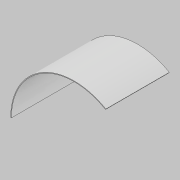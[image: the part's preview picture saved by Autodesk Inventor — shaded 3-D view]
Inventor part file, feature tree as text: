
AUTODESK INVENTOR PART (.ipt)
format: ipt  version: 2021 (Build 250183000, 183)  size: 96,256 bytes
history: native  units: mm
features: extrude x1, sketch x1
ambient origin geometry x8: Origin, YZ Plane, XZ Plane, XY Plane, X Axis, Y Axis, Z Axis, Center Point
bodies: Solid1 (feature_tree)
feature tree (2):
  extrude  "Extrusion1"  Depth=900.0mm
  sketch  "Sketch1"  dims[d0=10.0mm d1=900.0mm d2=0.0mm d4=900.0mm d5=0.0mm d6=120.0deg]
